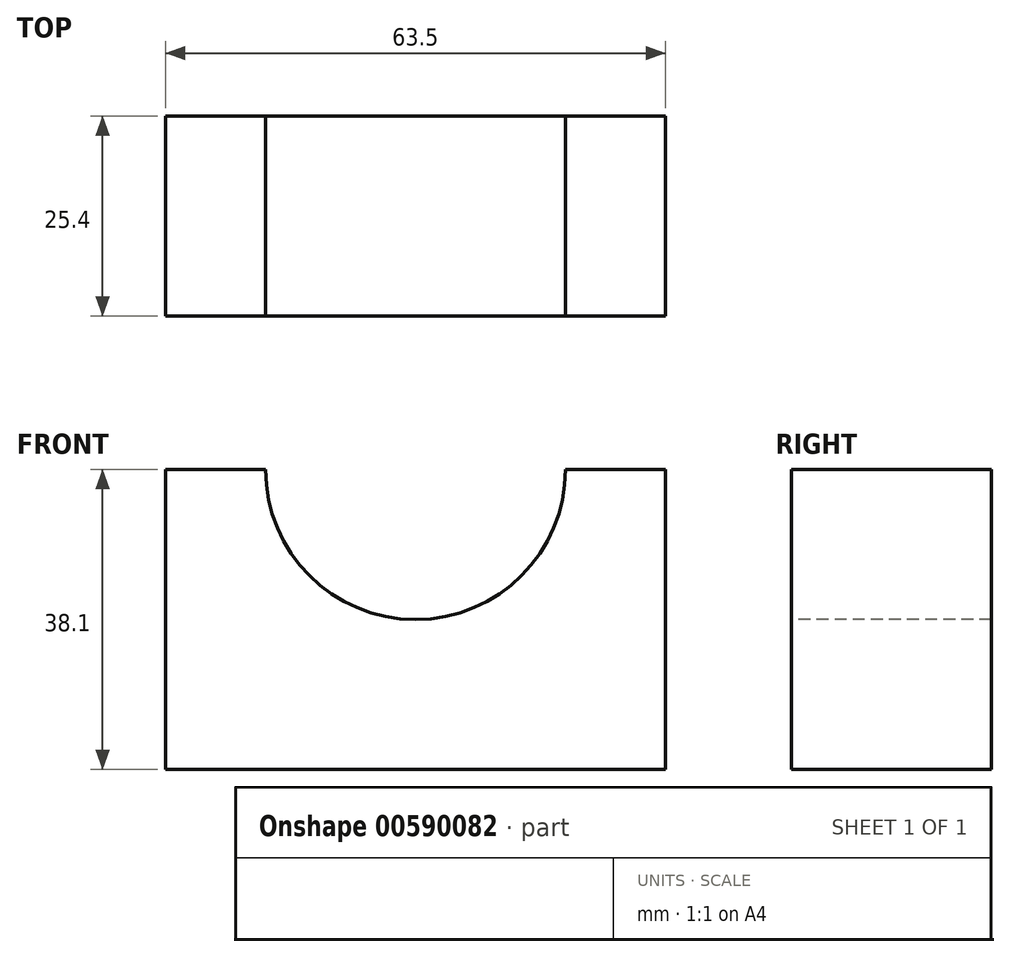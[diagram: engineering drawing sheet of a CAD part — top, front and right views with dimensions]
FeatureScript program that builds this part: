
annotation { "Feature Type Name" : "Feature", "Feature Type Description" : "" }
export const myFeature = defineFeature(function(context is Context, id is Id, definition is map)
    precondition{}
    {
        {
            var Q0;
            Q0=qCreatedBy(makeId("Front.planeOp"),FACE);
            var sketch = newSketch(context, id + "F0", { "sketchPlane" : qUnion([Q0])});
            skLineSegment(sketch, "E0", {"start": v(-65.6, 54.03) * mm, "end": v(-65.6, 15.93) * mm});
            skLineSegment(sketch, "E1", {"start": v(-65.6, 15.93) * mm, "end": v(-2.1, 15.93) * mm});
            skLineSegment(sketch, "E2", {"start": v(-65.6, 54.03) * mm, "end": v(-2.1, 54.03) * mm});
            skLineSegment(sketch, "E3", {"start": v(-2.1, 54.03) * mm, "end": v(-2.1, 15.93) * mm});
            skSolve(sketch);
        }
        {
            var Q0;
            Q0=makeQuery(id+"F0.imprint","IMPRINT",FACE,{"disambiguationData":[TD([[makeQuery(id+"F0.imprint","IMPRINT",EDGE,{"derivedFrom":sQuery(id+"F0.wireOp",EDGE,"E0")}),1.0]])]});
            extrude(context, id + "F1", {"entities" : qUnion([Q0]), "depth" : 25.4 * mm, "offsetDistance" : 25.4 * mm});
        }
        {
            var Q0;
            Q0=makeQuery(id+"F1.opExtrude","CAP_FACE",FACE,{"disambiguationData":[OSD([sQuery(id+"F0.wireOp",EDGE,"E0"),sQuery(id+"F0.wireOp",EDGE,"E1"),sQuery(id+"F0.wireOp",EDGE,"E2"),sQuery(id+"F0.wireOp",EDGE,"E3")])],"isStart":false});
            var sketch = newSketch(context, id + "F2", { "sketchPlane" : qUnion([Q0])});
            skCircle(sketch, "E4", {"center": v(-33.84, 54.03) * mm, "radius": 19.05 * mm});
            skSolve(sketch);
        }
        {
            var Q0;
            {var subQ0=sQuery(id+"F2.wireOp",EDGE,"E4");var subQ1=makeQuery(id+"F1.opExtrude","CAP_EDGE",EDGE,{"disambiguationData":[OSD([sQuery(id+"F0.wireOp",EDGE,"E2")])],"isStart":false});var subQ2=makeQuery(id+"F2.imprint","INTERSECT",VERTEX,{"disambiguationData":[OD(0.0)],"derivedFrom":[subQ1,subQ0]});Q0=makeQuery(id+"F2.imprint","IMPRINT",FACE,{"disambiguationData":[TD([[makeQuery(id+"F2.imprint","IMPRINT",EDGE,{"disambiguationData":[TD([[subQ2,-1.0]])],"derivedFrom":subQ0}),1.0]])]});}
            extrude(context, id + "F3", {"entities" : qUnion([Q0]), "operationType" : NewBodyOperationType.REMOVE, "endBound" : BoundingType.THROUGH_ALL, "oppositeDirection" : true, "depth" : 25.4 * mm, "offsetDistance" : 25.4 * mm});
        }
    });
